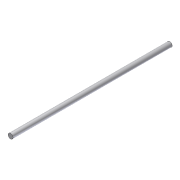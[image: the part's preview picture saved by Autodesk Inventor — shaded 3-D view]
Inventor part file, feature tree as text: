
AUTODESK INVENTOR PART (.ipt)
format: ipt  version: 2012 (Build 160160000, 160)  size: 63,488 bytes
history: native  units: in
note: dims shown in document units (in); Inventor stores cm internally (conversion verified against a paired STEP export)
features: extrude x1, plane x1, sketch x1, other x1
ambient origin geometry x8: Origin, YZ Plane, XZ Plane, XY Plane, X Axis, Y Axis, Z Axis, Center Point
bodies: Solid1 (feature_tree)
feature tree (4):
  extrude  "Extrusion1"  Depth=8.0in TaperAngle=0.0deg
  plane  "Work Plane1"
  sketch  "Sketch1"  dims[d0=0.25in d1=8.0in d2=0.0in d3=90.0deg]
  other  "Work Axis1"
